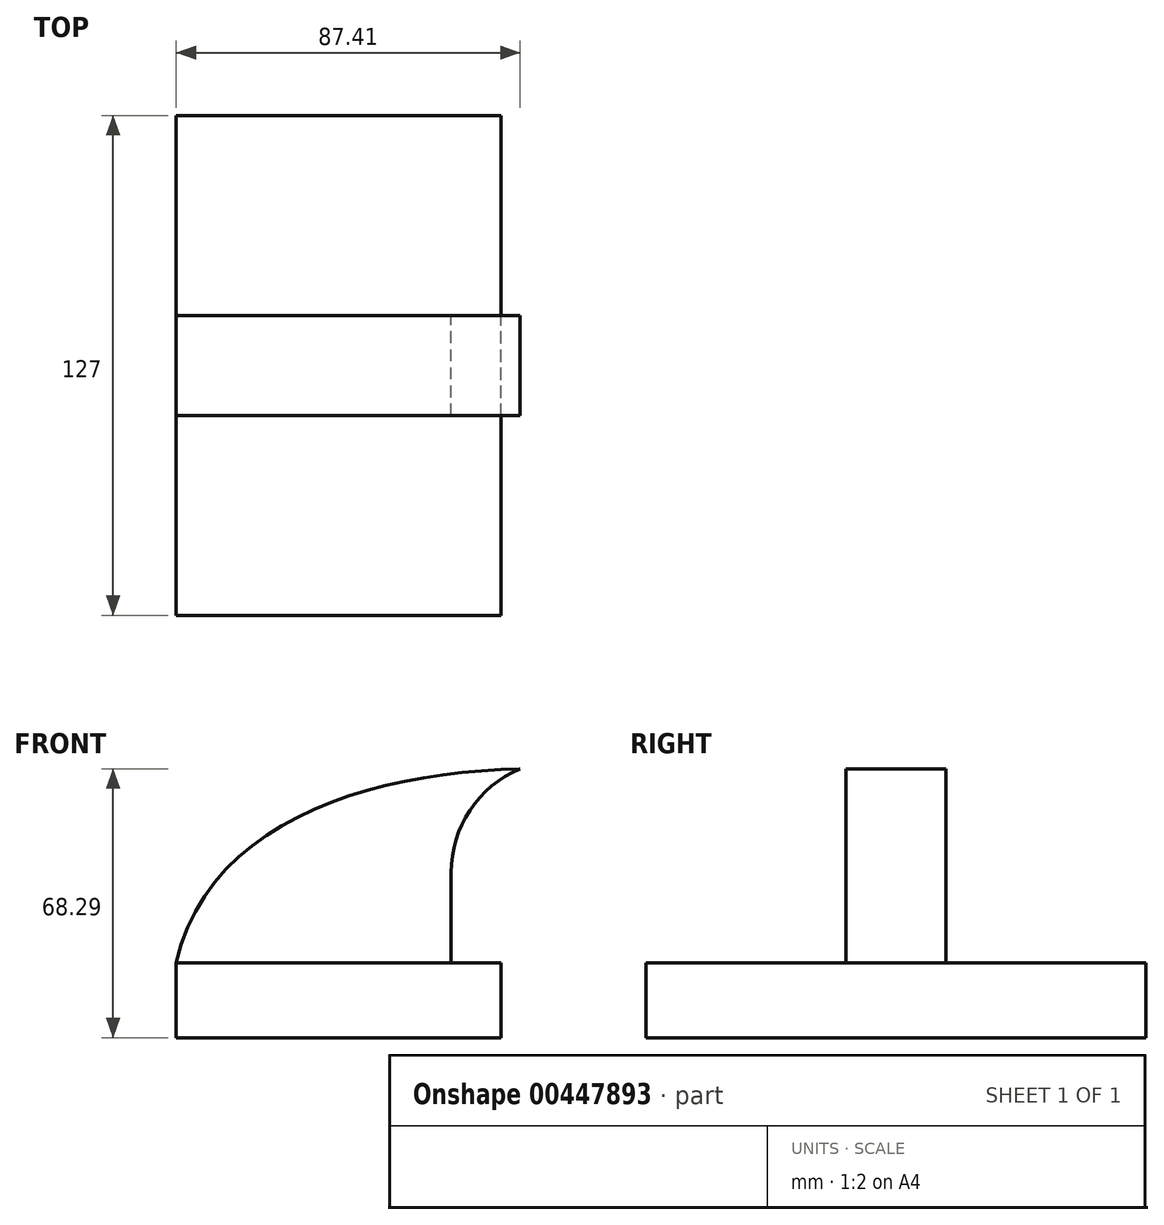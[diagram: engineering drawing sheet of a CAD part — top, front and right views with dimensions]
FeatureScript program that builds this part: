
annotation { "Feature Type Name" : "Feature", "Feature Type Description" : "" }
export const myFeature = defineFeature(function(context is Context, id is Id, definition is map)
    precondition{}
    {
        {
            var Q0;
            Q0=qCreatedBy(makeId("Front.planeOp"),FACE);
            var sketch = newSketch(context, id + "F0", { "sketchPlane" : qUnion([Q0])});
            skLineSegment(sketch, "E0.bottom", {"start": v(41.28, -9.52) * mm, "end": v(-41.28, -9.53) * mm});
            skLineSegment(sketch, "E0.top", {"start": v(41.28, 9.53) * mm, "end": v(-41.28, 9.53) * mm});
            skLineSegment(sketch, "E0.left", {"start": v(41.28, -9.52) * mm, "end": v(41.28, 9.53) * mm});
            skLineSegment(sketch, "E0.right", {"start": v(-41.28, -9.53) * mm, "end": v(-41.28, 9.53) * mm});
            skPoint(sketch, "E0.middle", {"position": v(0, 0) * mm});
            skLineSegment(sketch, "E1.bottom", {"start": v(111.12, 38.1) * mm, "end": v(60.32, 38.1) * mm});
            skLineSegment(sketch, "E1.top", {"start": v(111.12, 66.68) * mm, "end": v(60.32, 66.68) * mm});
            skLineSegment(sketch, "E1.left", {"start": v(111.12, 38.1) * mm, "end": v(111.12, 66.68) * mm});
            skLineSegment(sketch, "E1.right", {"start": v(60.32, 38.1) * mm, "end": v(60.32, 66.68) * mm});
            skPoint(sketch, "E1.middle", {"position": v(85.72, 52.39) * mm});
            skLineSegment(sketch, "E2", {"start": v(41.28, 9.53) * mm, "end": v(41.28, 32.4) * mm});
            skArc(sketch, "E3", {"start": v(41.27, 32.4) * mm, "mid": v(45.92, 43.63) * mm, "end": v(57.15, 48.28) * mm});
            skLineSegment(sketch, "E4", {"start": v(57.15, 48.28) * mm, "end": v(83.78, 48.28) * mm});
            skLineSegment(sketch, "E5.0", {"start": v(57.15, 60.98) * mm, "end": v(83.78, 60.98) * mm});
            skArc(sketch, "E5.1", {"start": v(28.57, 32.4) * mm, "mid": v(36.94, 52.6) * mm, "end": v(57.15, 60.98) * mm});
            skLineSegment(sketch, "E5.2", {"start": v(28.57, 9.53) * mm, "end": v(28.57, 32.4) * mm});
            skLineSegment(sketch, "E6", {"start": v(83.78, 66.68) * mm, "end": v(83.78, 38.1) * mm});
            skPoint(sketch, "E6.endSnap0", {"position": v(85.72, 38.1) * mm});
            skFitSpline(sketch, "E7", {"points": [v(-41.28, 9.52) * mm, v(46.13, 58.76) * mm], "startDerivative": vector(25.23, 109.38) * mm, "endDerivative": vector(111.9, 2.6) * mm});
            skSolve(sketch);
        }
        {
            var Q0;
            Q0=makeQuery(id+"F0.imprint","IMPRINT",FACE,{"disambiguationData":[TD([[makeQuery(id+"F0.imprint","IMPRINT",EDGE,{"derivedFrom":sQuery(id+"F0.wireOp",EDGE,"E0.bottom")}),-1.0]])]});
            extrude(context, id + "F1", {"entities" : qUnion([Q0]), "endBound" : BoundingType.SYMMETRIC, "depth" : 127 * mm});
        }
        {
            var Q0;
            {var subQ2=sQuery(id+"F0.wireOp",EDGE,"E5.2");Q0=makeQuery(id+"F0.imprint","IMPRINT",FACE,{"disambiguationData":[TD([[makeQuery(id+"F0.imprint","IMPRINT",EDGE,{"derivedFrom":subQ2}),1.0]])]});}
            extrude(context, id + "F2", {"entities" : qUnion([Q0]), "operationType" : NewBodyOperationType.ADD, "endBound" : BoundingType.SYMMETRIC, "depth" : 25.4 * mm});
        }
    });
